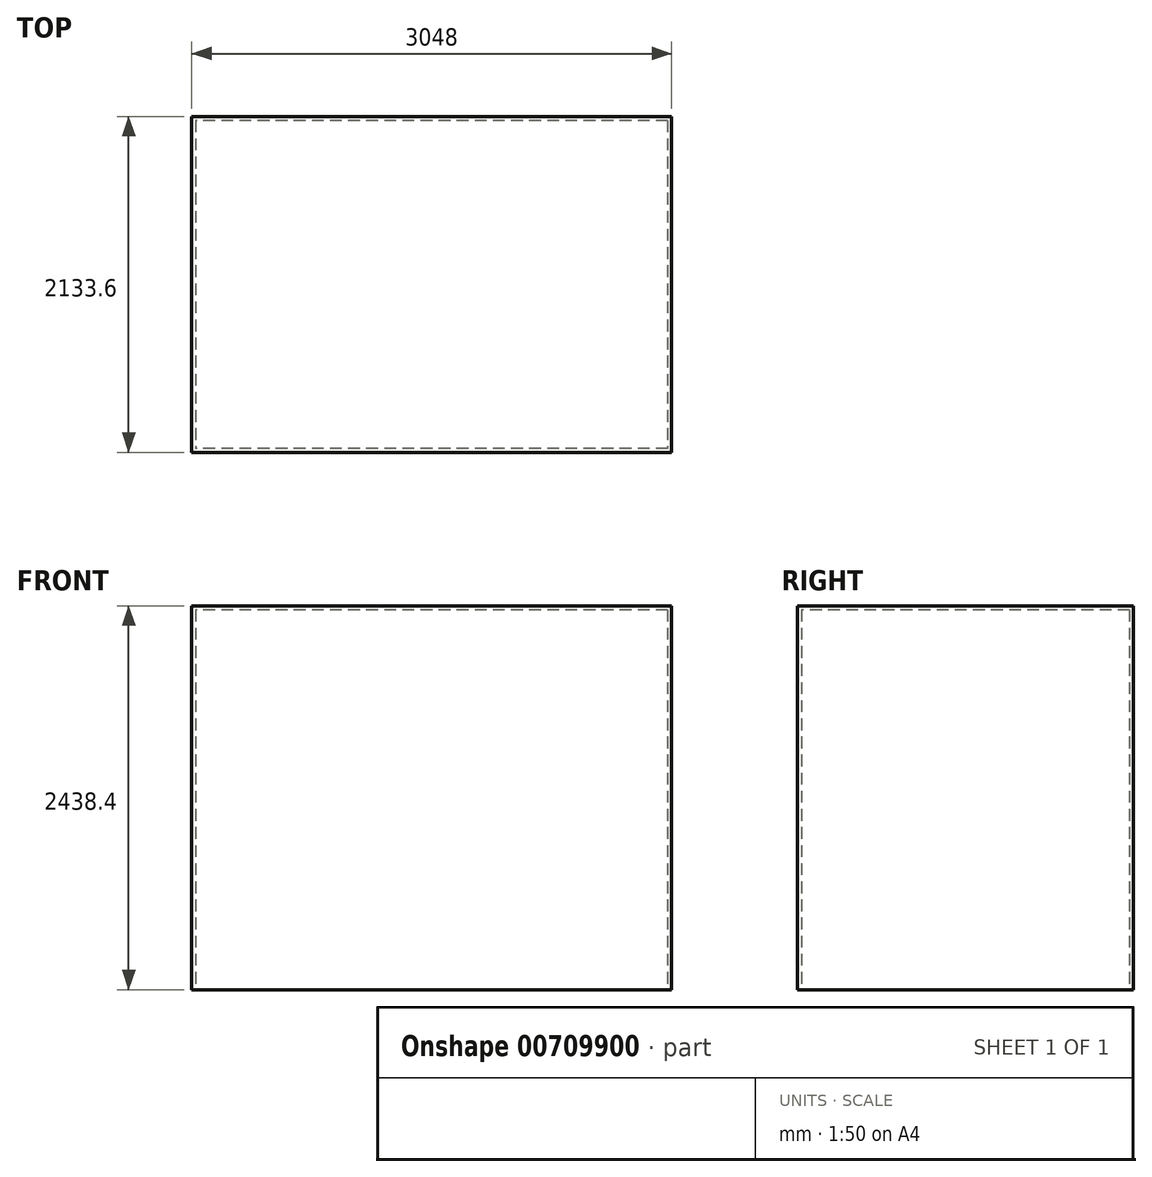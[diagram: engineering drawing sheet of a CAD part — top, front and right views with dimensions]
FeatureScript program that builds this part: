
annotation { "Feature Type Name" : "Feature", "Feature Type Description" : "" }
export const myFeature = defineFeature(function(context is Context, id is Id, definition is map)
    precondition{}
    {
        {
            var Q0;
            Q0=qCreatedBy(makeId("Top.planeOp"),FACE);
            var sketch = newSketch(context, id + "F0", { "sketchPlane" : qUnion([Q0])});
            skLineSegment(sketch, "E0.bottom", {"start": v(0, 0) * mm, "end": v(-3048, 0) * mm});
            skLineSegment(sketch, "E0.top", {"start": v(0, -2133.6) * mm, "end": v(-3048, -2133.6) * mm});
            skLineSegment(sketch, "E0.left", {"start": v(0, 0) * mm, "end": v(0, -2133.6) * mm});
            skLineSegment(sketch, "E0.right", {"start": v(-3048, 0) * mm, "end": v(-3048, -2133.6) * mm});
            skLineSegment(sketch, "E1", {"start": v(-1219.2, -2133.6) * mm, "end": v(-1219.2, 0) * mm});
            skLineSegment(sketch, "E2", {"start": v(-2438.4, -2133.6) * mm, "end": v(-2438.4, 0) * mm});
            skSolve(sketch);
        }
        {
            var Q0;
            Q0 = qSketchRegion(id + "F0", true);
            extrude(context, id + "F1", {"entities" : qUnion([Q0]), "depth" : 2438.4 * mm, "offsetDistance" : 25.4 * mm});
        }
        {
            var Q0;
            Q0=makeQuery(id+"F1.opExtrude","CAP_FACE",FACE,{"disambiguationData":[OSD([sQuery(id+"F0.wireOp",EDGE,"E0.bottom"),sQuery(id+"F0.wireOp",EDGE,"E0.top"),sQuery(id+"F0.wireOp",EDGE,"E0.left"),sQuery(id+"F0.wireOp",EDGE,"E0.right")])],"isStart":true});
            shell(context, id + "F2", {"entities" : qUnion([Q0]), "thickness" : 25.4 * mm});
        }
    });
